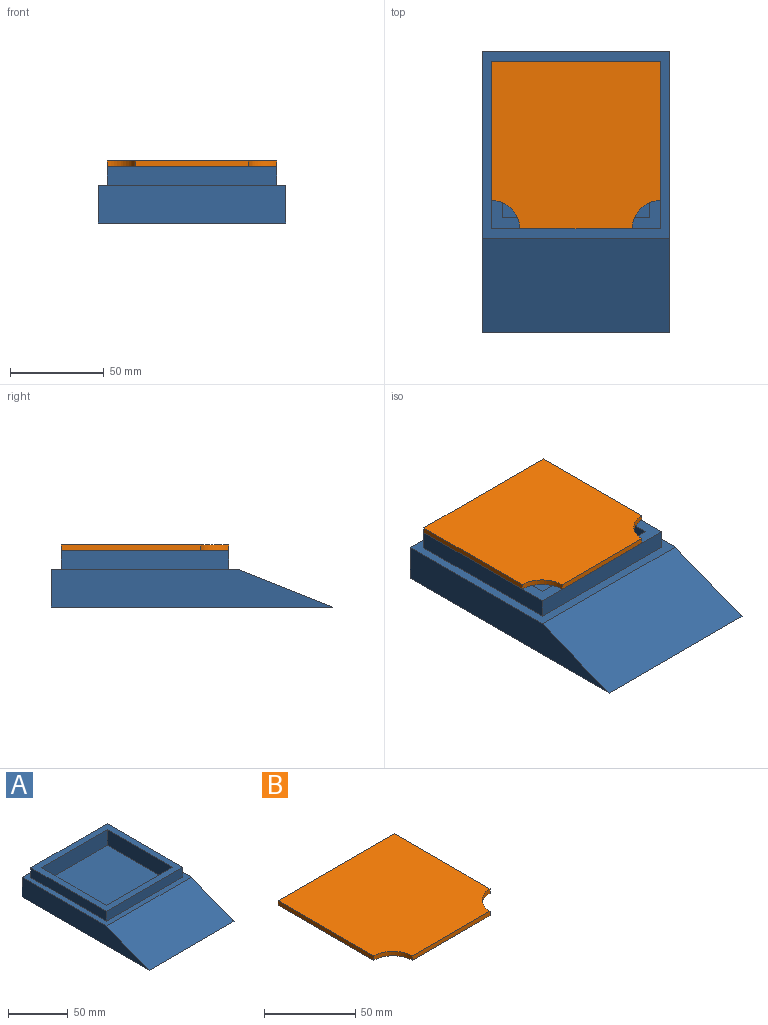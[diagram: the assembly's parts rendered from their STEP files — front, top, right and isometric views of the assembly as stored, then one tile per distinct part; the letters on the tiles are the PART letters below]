
ASSEMBLY  parts=2 mates=1
PART A: 16 faces, bbox 100x149.9x30 mm
  f0: plane 100x99.55mm, normal (0,0,1), area 1936.1mm2, adj f1,f2,f3,f5,f6,f7,f8,f13
  f1: plane 149.85x20mm, normal (-1,0,0), area 2494mm2, adj f0,f3,f4,f5
  f2: plane 149.85x20mm, normal (1,0,0), area 2494mm2, adj f0,f3,f4,f5
  f3: plane 100x20mm, normal (0,1,0), area 2000mm2, adj f0,f1,f2,f4
  f4: plane 149.85x100mm, normal (0,0,-1), area 14985.2mm2, adj f1,f2,f3,f5
  f5: plane 100x50.3mm, normal (0,-0.37,0.93), area 5413.3mm2, adj f0,f1,f2,f4
  f6: plane 89.1x10mm, normal (-1,0,0), area 891mm2, adj f0,f7,f13,f14
  f7: plane 90x10mm, normal (0,-1,0), area 900mm2, adj f0,f6,f8,f14
  f8: plane 89.1x10mm, normal (1,0,0), area 891mm2, adj f0,f7,f13,f14
  f9: plane 77.94x16mm, normal (0,1,0), area 1247.1mm2, adj f10,f12,f14,f15
  f10: plane 76.88x16mm, normal (1,0,0), area 1230.1mm2, adj f9,f11,f14,f15
  f11: plane 77.94x16mm, normal (0,-1,0), area 1247.1mm2, adj f10,f12,f14,f15
  f12: plane 76.88x16mm, normal (-1,0,0), area 1230.1mm2, adj f9,f11,f14,f15
  f13: plane 90x10mm, normal (0,1,0), area 900mm2, adj f0,f6,f8,f14
  f14: plane 90x89.1mm, normal (0,0,1), area 2026.7mm2, adj f6,f7,f8,f9,f10,f11,f12,f13
  f15: plane 77.94x76.88mm, normal (0,0,1), area 5992.1mm2, adj f9,f10,f11,f12
PART B: 8 faces, bbox 90x89x3 mm
  f0: plane 60x3mm, normal (0,-1,0), area 180mm2, adj f4,f5,f6,f7
  f1: plane 90x3mm, normal (0,1,0), area 270mm2, adj f2,f3,f4,f5
  f2: plane 74x3mm, normal (-1,0,0), area 222mm2, adj f1,f4,f5,f7
  f3: plane 74x3mm, normal (1,0,0), area 222mm2, adj f1,f4,f5,f6
  f4: plane 90x89mm, normal (0,0,1), area 7656.6mm2, adj f0,f1,f2,f3,f6,f7
  f5: plane 90x89mm, normal (0,0,-1), area 7656.6mm2, adj f0,f1,f2,f3,f6,f7
  f6: cylinder r=15mm len=15mm, axis (0,0,1), area 70.7mm2, adj f0,f3,f4,f5
  f7: cylinder r=15mm len=15mm, axis (0,0,1), area 70.7mm2, adj f0,f2,f4,f5
PLACE A t=(-143.05,-81.05,-8.11)mm
PLACE B t=(-282.16,-82.95,21.89)mm
MATE fastened B.f5 <-> A.f14  axis (0,0,-1) through (-188.05,-36.5,21.89)mm
